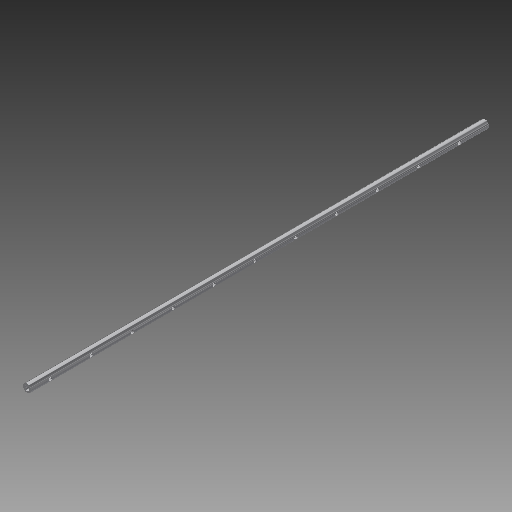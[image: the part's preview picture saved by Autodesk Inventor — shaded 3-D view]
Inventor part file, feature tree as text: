
AUTODESK INVENTOR PART (.ipt)
format: ipt  version: 2019 (Build 230136000, 136)  size: 170,496 bytes
history: native  units: mm
features: extrude x2, sketch x2, projected_geometry x1
ambient origin geometry x8: Origin, YZ Plane, XZ Plane, XY Plane, X Axis, Y Axis, Z Axis, Center Point
bodies: Solid1 (feature_tree)
feature tree (5):
  extrude  "Extrusion1"  Depth=3.0mm
  extrude  "Extrusion2"  Depth=10.0mm
  sketch  "Sketch1"  dims[d0=5.0mm d1=3.0mm]
  sketch  "Sketch2"  dims[d2=280.0mm d3=0.0mm d4=12.0mm d5=2.05mm d6=110.0mm d8=25.0mm d9=10.0mm d11=10.0mm d13=280.0mm d14=0.0mm]
  projected_geometry  "Projected Loop1"
